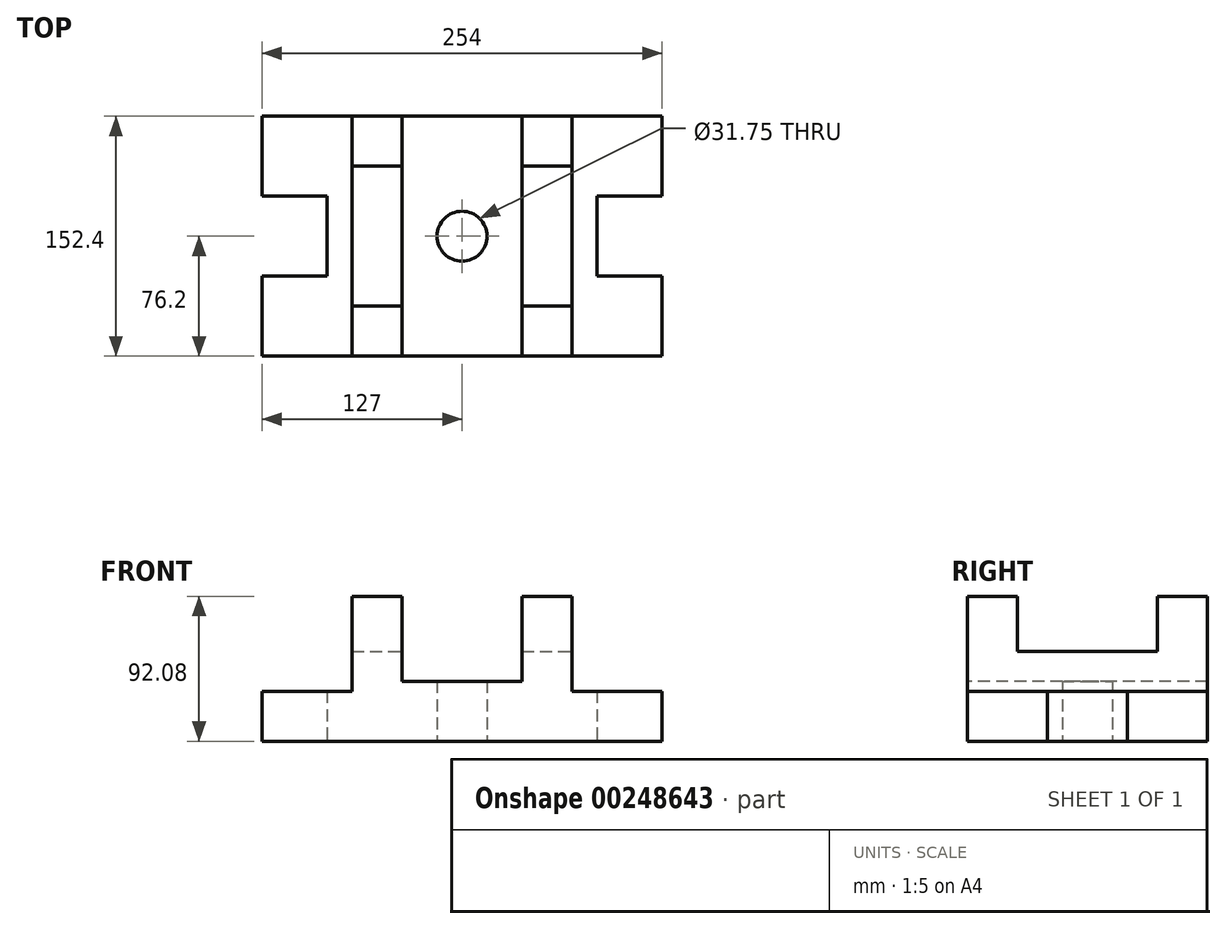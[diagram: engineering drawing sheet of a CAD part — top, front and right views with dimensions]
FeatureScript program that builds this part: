
annotation { "Feature Type Name" : "Feature", "Feature Type Description" : "" }
export const myFeature = defineFeature(function(context is Context, id is Id, definition is map)
    precondition{}
    {
        {
            var Q0;
            Q0=qCreatedBy(makeId("Top.planeOp"),FACE);
            var sketch = newSketch(context, id + "F0", { "sketchPlane" : qUnion([Q0])});
            skLineSegment(sketch, "E0.bottom", {"start": v(-85.73, 50.8) * mm, "end": v(85.72, 50.8) * mm});
            skLineSegment(sketch, "E0.top", {"start": v(-85.72, -101.6) * mm, "end": v(85.72, -101.6) * mm});
            skLineSegment(sketch, "E0.left", {"start": v(-85.73, 50.8) * mm, "end": v(-85.73, -101.6) * mm});
            skLineSegment(sketch, "E0.right", {"start": v(85.72, 50.8) * mm, "end": v(85.72, -101.6) * mm});
            skLineSegment(sketch, "E1.bottom", {"start": v(85.72, 50.8) * mm, "end": v(127, 50.8) * mm});
            skLineSegment(sketch, "E1.top", {"start": v(85.72, 0) * mm, "end": v(127, 0) * mm});
            skLineSegment(sketch, "E1.left", {"start": v(85.72, 50.8) * mm, "end": v(85.72, 0) * mm});
            skLineSegment(sketch, "E1.right", {"start": v(127, 50.8) * mm, "end": v(127, 0) * mm});
            skLineSegment(sketch, "E2.bottom", {"start": v(85.72, -101.6) * mm, "end": v(127, -101.6) * mm});
            skLineSegment(sketch, "E2.top", {"start": v(85.72, -50.8) * mm, "end": v(127, -50.8) * mm});
            skLineSegment(sketch, "E2.left", {"start": v(85.73, -101.6) * mm, "end": v(85.72, -50.8) * mm});
            skLineSegment(sketch, "E2.right", {"start": v(127, -101.6) * mm, "end": v(127, -50.8) * mm});
            skLineSegment(sketch, "E3.bottom", {"start": v(-85.72, -101.6) * mm, "end": v(-127, -101.6) * mm});
            skLineSegment(sketch, "E3.top", {"start": v(-85.72, -50.8) * mm, "end": v(-127, -50.8) * mm});
            skLineSegment(sketch, "E3.left", {"start": v(-85.72, -101.6) * mm, "end": v(-85.72, -50.8) * mm});
            skLineSegment(sketch, "E3.right", {"start": v(-127, -101.6) * mm, "end": v(-127, -50.8) * mm});
            skLineSegment(sketch, "E4.bottom", {"start": v(-85.73, 50.8) * mm, "end": v(-127, 50.8) * mm});
            skLineSegment(sketch, "E4.top", {"start": v(-85.73, 0) * mm, "end": v(-127, 0) * mm});
            skLineSegment(sketch, "E4.left", {"start": v(-85.73, 50.8) * mm, "end": v(-85.73, 0) * mm});
            skLineSegment(sketch, "E4.right", {"start": v(-127, 50.8) * mm, "end": v(-127, 0) * mm});
            skLineSegment(sketch, "E5", {"start": v(-69.85, 50.8) * mm, "end": v(-69.85, -101.6) * mm});
            skLineSegment(sketch, "E6", {"start": v(-38.1, 50.8) * mm, "end": v(-38.1, -101.6) * mm});
            skLineSegment(sketch, "E7", {"start": v(69.85, 50.8) * mm, "end": v(69.85, -101.6) * mm});
            skLineSegment(sketch, "E8", {"start": v(38.1, 50.8) * mm, "end": v(38.1, -101.6) * mm});
            skLineSegment(sketch, "E9", {"start": v(38.1, 19.05) * mm, "end": v(69.85, 19.05) * mm});
            skLineSegment(sketch, "E10", {"start": v(-69.85, 19.05) * mm, "end": v(-38.1, 19.05) * mm});
            skLineSegment(sketch, "E11", {"start": v(-69.85, -69.85) * mm, "end": v(-38.1, -69.85) * mm});
            skLineSegment(sketch, "E12", {"start": v(38.1, -69.85) * mm, "end": v(69.85, -69.85) * mm});
            skCircle(sketch, "E13", {"center": v(0, -25.4) * mm, "radius": 15.88 * mm});
            skSolve(sketch);
        }
        {
            var Q0;
            Q0=makeQuery(id+"F0.imprint","IMPRINT",FACE,{"disambiguationData":[TD([[makeQuery(id+"F0.imprint","IMPRINT",EDGE,{"derivedFrom":sQuery(id+"F0.wireOp",EDGE,"E13")}),-1.0]])]});
            extrude(context, id + "F1", {"entities" : qUnion([Q0]), "depth" : 38.1 * mm});
        }
        {
            var Q0;
            {var subQ5=sQuery(id+"F0.wireOp",EDGE,"E10");Q0=makeQuery(id+"F0.imprint","IMPRINT",FACE,{"disambiguationData":[TD([[makeQuery(id+"F0.imprint","IMPRINT",EDGE,{"derivedFrom":subQ5}),1.0]])]});}
            var Q1;
            {var subQ5=sQuery(id+"F0.wireOp",EDGE,"E11");Q1=makeQuery(id+"F0.imprint","IMPRINT",FACE,{"disambiguationData":[TD([[makeQuery(id+"F0.imprint","IMPRINT",EDGE,{"derivedFrom":subQ5}),-1.0]])]});}
            var Q2;
            {var subQ5=sQuery(id+"F0.wireOp",EDGE,"E12");Q2=makeQuery(id+"F0.imprint","IMPRINT",FACE,{"disambiguationData":[TD([[makeQuery(id+"F0.imprint","IMPRINT",EDGE,{"derivedFrom":subQ5}),-1.0]])]});}
            var Q3;
            {var subQ5=sQuery(id+"F0.wireOp",EDGE,"E9");Q3=makeQuery(id+"F0.imprint","IMPRINT",FACE,{"disambiguationData":[TD([[makeQuery(id+"F0.imprint","IMPRINT",EDGE,{"derivedFrom":subQ5}),1.0]])]});}
            extrude(context, id + "F2", {"entities" : qUnion([Q0, Q1, Q2, Q3]), "operationType" : NewBodyOperationType.ADD, "depth" : 92.07 * mm});
        }
        {
            var Q0;
            {var subQ0=sQuery(id+"F0.wireOp",EDGE,"E9");Q0=makeQuery(id+"F0.imprint","IMPRINT",FACE,{"disambiguationData":[TD([[makeQuery(id+"F0.imprint","IMPRINT",EDGE,{"derivedFrom":subQ0}),-1.0]])]});}
            var Q1;
            {var subQ0=sQuery(id+"F0.wireOp",EDGE,"E10");Q1=makeQuery(id+"F0.imprint","IMPRINT",FACE,{"disambiguationData":[TD([[makeQuery(id+"F0.imprint","IMPRINT",EDGE,{"derivedFrom":subQ0}),-1.0]])]});}
            extrude(context, id + "F3", {"entities" : qUnion([Q0, Q1]), "operationType" : NewBodyOperationType.ADD, "depth" : 57.15 * mm});
        }
        {
            var Q0;
            Q0=makeQuery(id+"F0.imprint","IMPRINT",FACE,{"disambiguationData":[TD([[makeQuery(id+"F0.imprint","IMPRINT",EDGE,{"derivedFrom":sQuery(id+"F0.wireOp",EDGE,"E1.bottom")}),-1.0]])]});
            var Q1;
            Q1=makeQuery(id+"F0.imprint","IMPRINT",FACE,{"disambiguationData":[TD([[makeQuery(id+"F0.imprint","IMPRINT",EDGE,{"derivedFrom":sQuery(id+"F0.wireOp",EDGE,"E2.bottom")}),1.0]])]});
            var Q2;
            Q2=makeQuery(id+"F0.imprint","IMPRINT",FACE,{"disambiguationData":[TD([[makeQuery(id+"F0.imprint","IMPRINT",EDGE,{"derivedFrom":sQuery(id+"F0.wireOp",EDGE,"E0.right")}),-1.0]])]});
            var Q3;
            Q3=makeQuery(id+"F0.imprint","IMPRINT",FACE,{"disambiguationData":[TD([[makeQuery(id+"F0.imprint","IMPRINT",EDGE,{"derivedFrom":sQuery(id+"F0.wireOp",EDGE,"E0.left")}),1.0]])]});
            var Q4;
            Q4=makeQuery(id+"F0.imprint","IMPRINT",FACE,{"disambiguationData":[TD([[makeQuery(id+"F0.imprint","IMPRINT",EDGE,{"derivedFrom":sQuery(id+"F0.wireOp",EDGE,"E4.bottom")}),1.0]])]});
            var Q5;
            Q5=makeQuery(id+"F0.imprint","IMPRINT",FACE,{"disambiguationData":[TD([[makeQuery(id+"F0.imprint","IMPRINT",EDGE,{"derivedFrom":sQuery(id+"F0.wireOp",EDGE,"E3.bottom")}),-1.0]])]});
            extrude(context, id + "F4", {"entities" : qUnion([Q0, Q1, Q2, Q3, Q4, Q5]), "operationType" : NewBodyOperationType.ADD, "depth" : 31.75 * mm});
        }
    });
